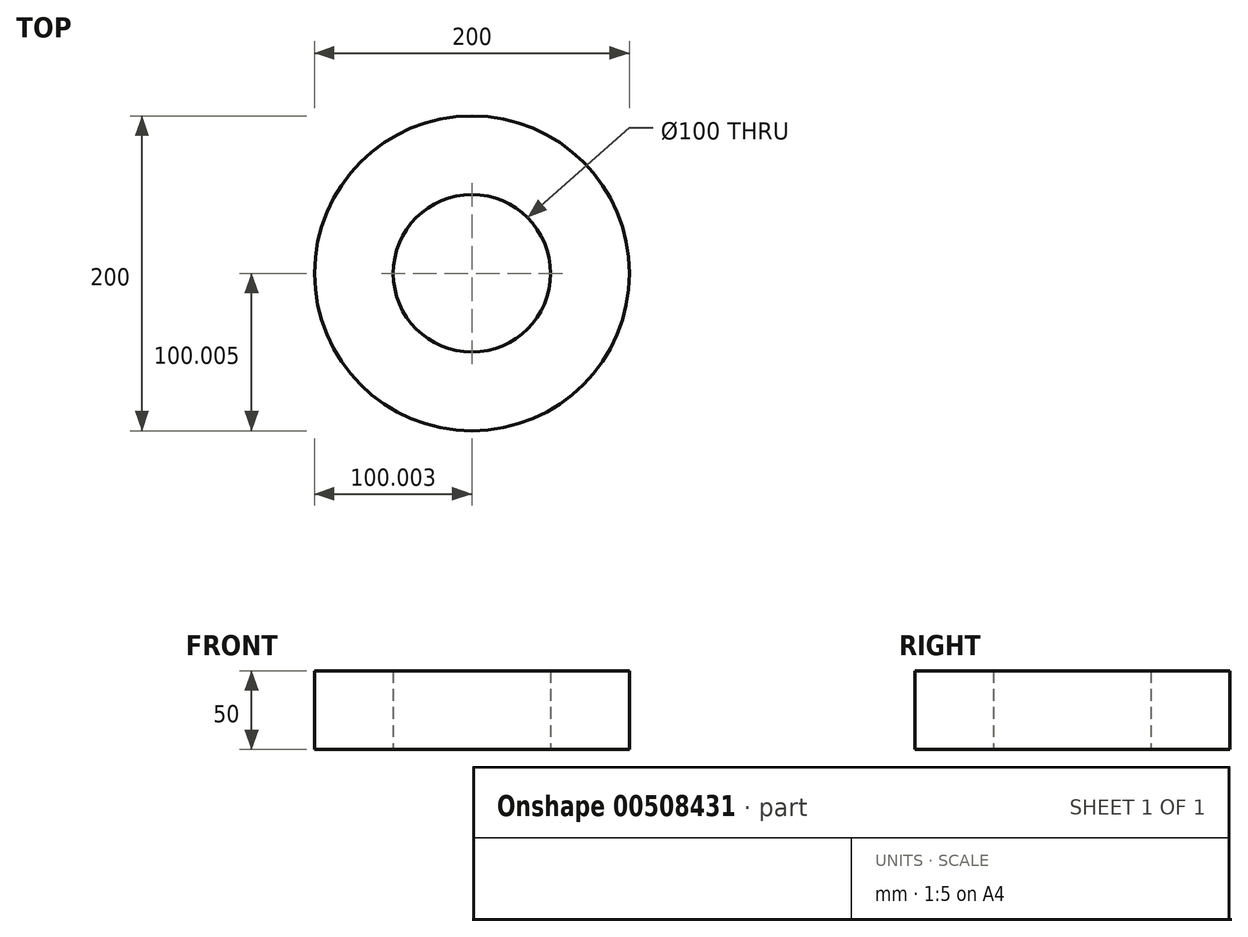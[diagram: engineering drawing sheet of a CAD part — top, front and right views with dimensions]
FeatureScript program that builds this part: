
annotation { "Feature Type Name" : "Feature", "Feature Type Description" : "" }
export const myFeature = defineFeature(function(context is Context, id is Id, definition is map)
    precondition{}
    {
        {
            var Q0;
            Q0=qCreatedBy(makeId("Top.planeOp"),FACE);
            var sketch = newSketch(context, id + "F0", { "sketchPlane" : qUnion([Q0])});
            skCircle(sketch, "E0", {"center": v(-13.19, -23) * mm, "radius": 100 * mm});
            skCircle(sketch, "E1", {"center": v(-13.19, -23) * mm, "radius": 50 * mm});
            skSolve(sketch);
        }
        {
            var Q0;
            Q0 = qSketchRegion(id + "F0", true);
            extrude(context, id + "F1", {"entities" : qUnion([Q0]), "depth" : 50 * mm});
        }
    });
